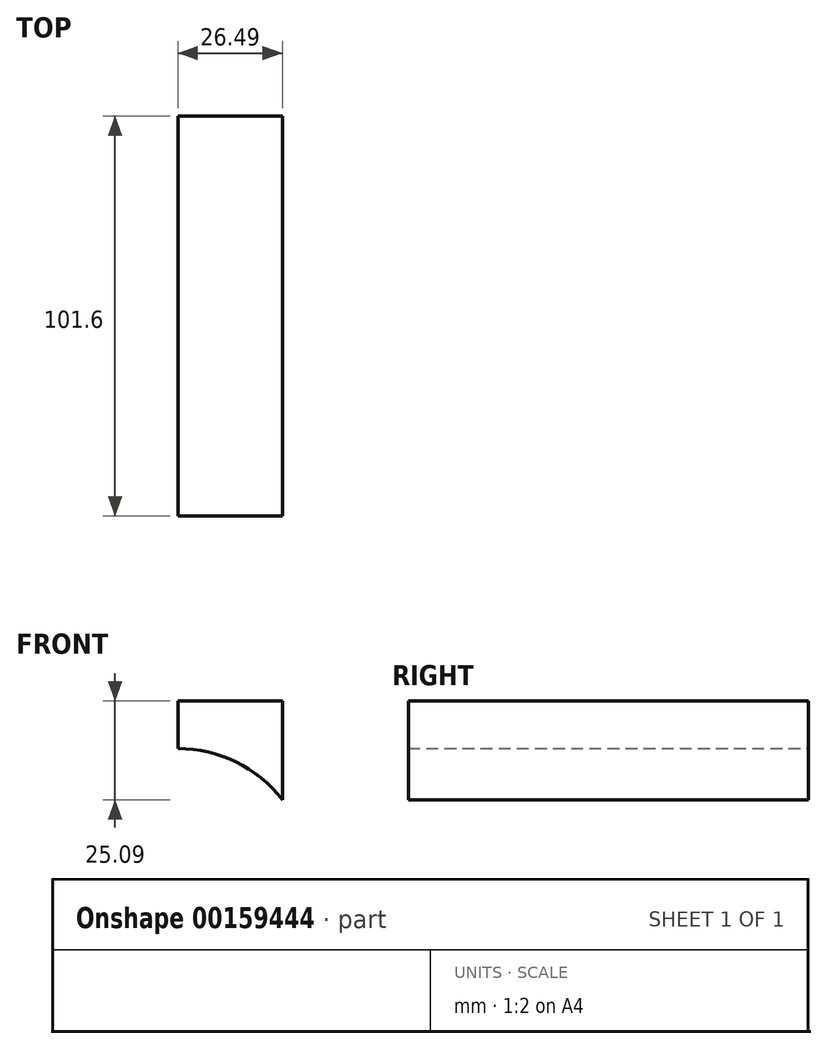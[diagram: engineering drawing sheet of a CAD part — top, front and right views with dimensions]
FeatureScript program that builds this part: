
annotation { "Feature Type Name" : "Feature", "Feature Type Description" : "" }
export const myFeature = defineFeature(function(context is Context, id is Id, definition is map)
    precondition{}
    {
        {
            var Q0;
            Q0=qCreatedBy(makeId("Front.planeOp"),FACE);
            var sketch = newSketch(context, id + "F0", { "sketchPlane" : qUnion([Q0])});
            skCircle(sketch, "E0", {"center": v(0, 0) * mm, "radius": 33.45 * mm});
            skLineSegment(sketch, "E1", {"start": v(0, 33.45) * mm, "end": v(0, 45.52) * mm});
            skLineSegment(sketch, "E2", {"start": v(0, 45.52) * mm, "end": v(26.49, 45.52) * mm});
            skLineSegment(sketch, "E3", {"start": v(26.49, 45.52) * mm, "end": v(26.49, 20.43) * mm});
            skSolve(sketch);
        }
        {
            var Q0;
            {var subQ0=sQuery(id+"F0.wireOp",EDGE,"E1");Q0=makeQuery(id+"F0.imprint","IMPRINT",FACE,{"disambiguationData":[TD([[makeQuery(id+"F0.imprint","IMPRINT",EDGE,{"derivedFrom":subQ0}),-1.0]])]});}
            extrude(context, id + "F1", {"entities" : qUnion([Q0]), "depth" : 101.6 * mm});
        }
    });
